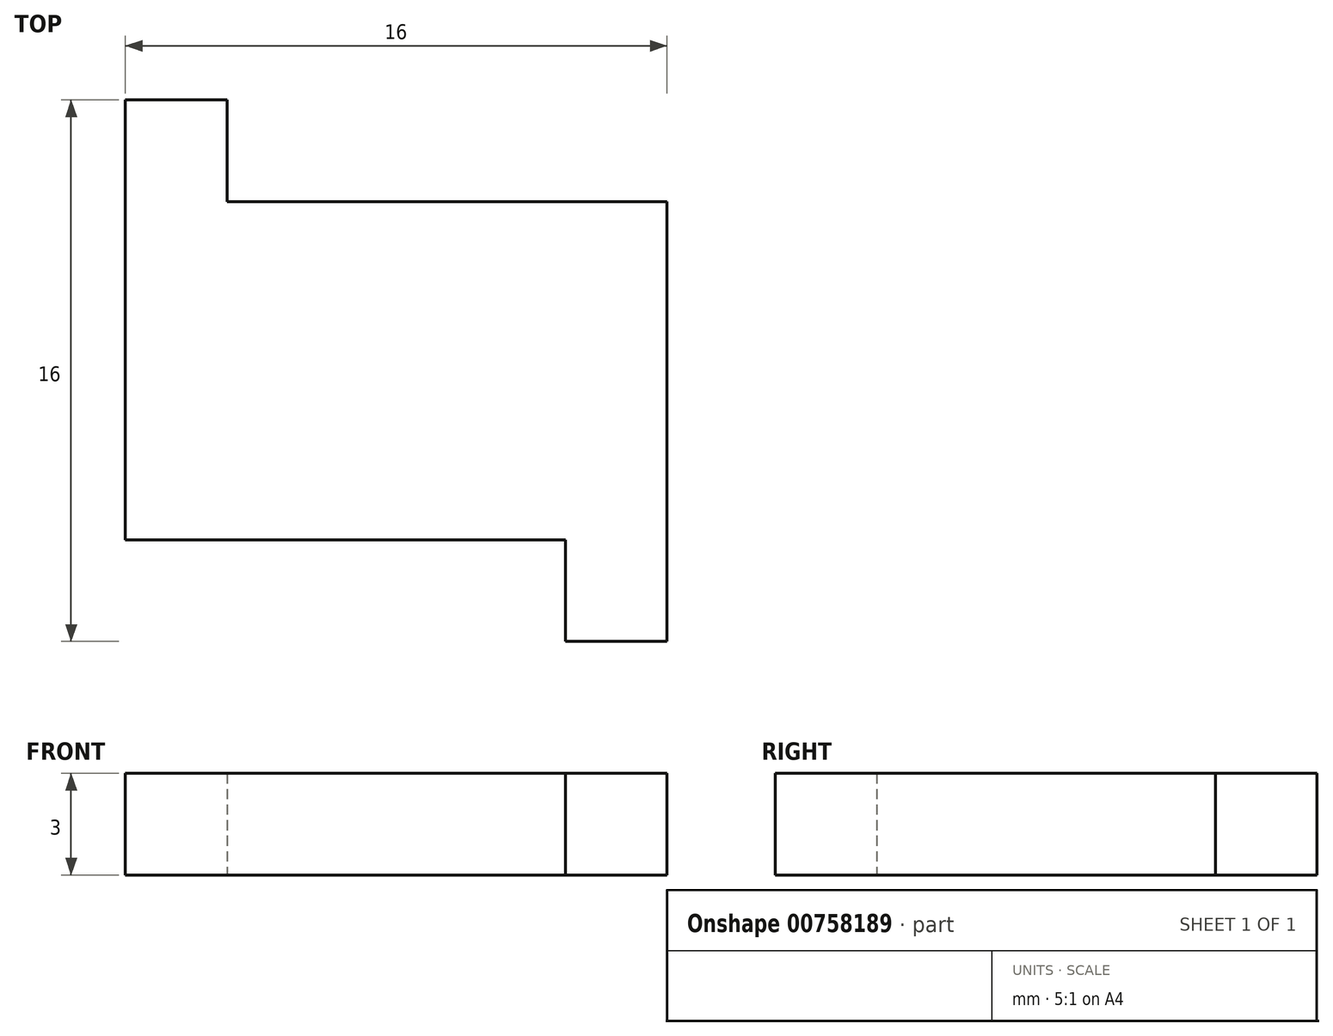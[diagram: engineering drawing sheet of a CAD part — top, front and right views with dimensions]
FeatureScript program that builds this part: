
annotation { "Feature Type Name" : "Feature", "Feature Type Description" : "" }
export const myFeature = defineFeature(function(context is Context, id is Id, definition is map)
    precondition{}
    {
        {
            var Q0;
            Q0=qCreatedBy(makeId("Top.planeOp"),FACE);
            var sketch = newSketch(context, id + "F0", { "sketchPlane" : qUnion([Q0])});
            skLineSegment(sketch, "E0.bottom", {"start": v(5, -5) * mm, "end": v(-5, -5) * mm});
            skLineSegment(sketch, "E0.top", {"start": v(5, 5) * mm, "end": v(-5, 5) * mm});
            skLineSegment(sketch, "E0.left", {"start": v(5, -5) * mm, "end": v(5, 5) * mm});
            skLineSegment(sketch, "E0.right", {"start": v(-5, -5) * mm, "end": v(-5, 5) * mm});
            skPoint(sketch, "E0.middle", {"position": v(0, 0) * mm});
            skSolve(sketch);
        }
        {
            var Q0;
            Q0=qCreatedBy(makeId("Front.planeOp"),FACE);
            var sketch = newSketch(context, id + "F1", { "sketchPlane" : qUnion([Q0])});
            skLineSegment(sketch, "E1.bottom", {"start": v(5, -5) * mm, "end": v(-5, -5) * mm});
            skLineSegment(sketch, "E1.top", {"start": v(5, 5) * mm, "end": v(-5, 5) * mm});
            skLineSegment(sketch, "E1.left", {"start": v(5, -5) * mm, "end": v(5, 5) * mm});
            skLineSegment(sketch, "E1.right", {"start": v(-5, -5) * mm, "end": v(-5, 5) * mm});
            skPoint(sketch, "E1.middle", {"position": v(0, 0) * mm});
            skSolve(sketch);
        }
        {
            var Q0;
            Q0=sQuery(id+"F1.wireOp",VERTEX,"E1.right.end");
            var Q1;
            Q1=sQuery(id+"F1.wireOp",EDGE,"E1.left");
            cPlane(context, id + "F2", {"entities" : qUnion([Q0, Q1]), "cplaneType" : CPlaneType.LINE_POINT, "offset" : 0 * mm, "width" : 150 * mm, "height" : 150 * mm});
        }
        {
            var Q0;
            Q0=qCreatedBy(id+"F2.planeOp",FACE);
            var sketch = newSketch(context, id + "F3", { "sketchPlane" : qUnion([Q0])});
            skPoint(sketch, "E2.0", {"position": v(-5, -5) * mm});
            skPoint(sketch, "E3.0", {"position": v(5, 5) * mm});
            skLineSegment(sketch, "E4.bottom", {"start": v(-8, -5) * mm, "end": v(8, -5) * mm});
            skLineSegment(sketch, "E4.top", {"start": v(-5, 5) * mm, "end": v(5, 5) * mm});
            skLineSegment(sketch, "E4.left", {"start": v(-5, -8) * mm, "end": v(-5, 5) * mm});
            skLineSegment(sketch, "E4.right", {"start": v(5, -8) * mm, "end": v(5, 5) * mm});
            skLineSegment(sketch, "E5.bottom", {"start": v(-8, 5) * mm, "end": v(8, 5) * mm});
            skLineSegment(sketch, "E5.top", {"start": v(-8, 8) * mm, "end": v(8, 8) * mm});
            skLineSegment(sketch, "E5.left", {"start": v(-5, 5) * mm, "end": v(-5, 8) * mm});
            skLineSegment(sketch, "E5.right", {"start": v(5, 5) * mm, "end": v(5, 8) * mm});
            skLineSegment(sketch, "E6.0", {"start": v(-8, -8) * mm, "end": v(-8, 8) * mm});
            skLineSegment(sketch, "E7.0", {"start": v(-8, -8) * mm, "end": v(8, -8) * mm});
            skLineSegment(sketch, "E8.0", {"start": v(8, -8) * mm, "end": v(8, 8) * mm});
            skLineSegment(sketch, "E9", {"start": v(-8, 0) * mm, "end": v(-5, 0) * mm});
            skLineSegment(sketch, "E10", {"start": v(0, 8) * mm, "end": v(0, 5) * mm});
            skLineSegment(sketch, "E11", {"start": v(0, -5) * mm, "end": v(0, -8) * mm});
            skLineSegment(sketch, "E12", {"start": v(8, 0) * mm, "end": v(5, 0) * mm});
            skSolve(sketch);
        }
        {
            var Q0;
            {var subQ2=sQuery(id+"F3.wireOp",EDGE,"E4.bottom");var subQ4=makeQuery(id+"F3.imprint","INTERSECT",VERTEX,{"derivedFrom":[subQ2,sQuery(id+"F3.wireOp",EDGE,"E11")]});Q0=makeQuery(id+"F3.imprint","IMPRINT",FACE,{"disambiguationData":[TD([[makeQuery(id+"F3.imprint","IMPRINT",EDGE,{"disambiguationData":[TD([[subQ4,1.0]])],"derivedFrom":subQ2}),1.0]])]});}
            var Q1;
            {var subQ3=sQuery(id+"F3.wireOp",EDGE,"E9");Q1=makeQuery(id+"F3.imprint","IMPRINT",FACE,{"disambiguationData":[TD([[makeQuery(id+"F3.imprint","IMPRINT",EDGE,{"derivedFrom":subQ3}),1.0]])]});}
            var Q2;
            {var subQ0=sQuery(id+"F3.wireOp",EDGE,"E5.left");Q2=makeQuery(id+"F3.imprint","IMPRINT",FACE,{"disambiguationData":[TD([[makeQuery(id+"F3.imprint","IMPRINT",EDGE,{"derivedFrom":subQ0}),1.0]])]});}
            var Q3;
            {var subQ5=sQuery(id+"F3.wireOp",EDGE,"E12");Q3=makeQuery(id+"F3.imprint","IMPRINT",FACE,{"disambiguationData":[TD([[makeQuery(id+"F3.imprint","IMPRINT",EDGE,{"derivedFrom":subQ5}),1.0]])]});}
            var Q4;
            {var subQ0=sQuery(id+"F3.wireOp",EDGE,"E8.0");var subQ1=sQuery(id+"F3.wireOp",EDGE,"E4.bottom");var subQ2=makeQuery(id+"F3.imprint","INTERSECT",VERTEX,{"derivedFrom":[subQ1,subQ0]});Q4=makeQuery(id+"F3.imprint","IMPRINT",FACE,{"disambiguationData":[TD([[makeQuery(id+"F3.imprint","IMPRINT",EDGE,{"disambiguationData":[TD([[subQ2,1.0]])],"derivedFrom":subQ1}),-1.0]])]});}
            var Q5;
            {var subQ5=sQuery(id+"F3.wireOp",EDGE,"E9");Q5=makeQuery(id+"F3.imprint","IMPRINT",FACE,{"disambiguationData":[TD([[makeQuery(id+"F3.imprint","IMPRINT",EDGE,{"derivedFrom":subQ5}),-1.0]])]});}
            var Q6;
            {var subQ3=sQuery(id+"F3.wireOp",EDGE,"E12");Q6=makeQuery(id+"F3.imprint","IMPRINT",FACE,{"disambiguationData":[TD([[makeQuery(id+"F3.imprint","IMPRINT",EDGE,{"derivedFrom":subQ3}),-1.0]])]});}
            extrude(context, id + "F4", {"entities" : qUnion([Q0, Q1, Q2, Q3, Q4, Q5, Q6]), "depth" : 3 * mm, "offsetDistance" : 25 * mm});
        }
    });
